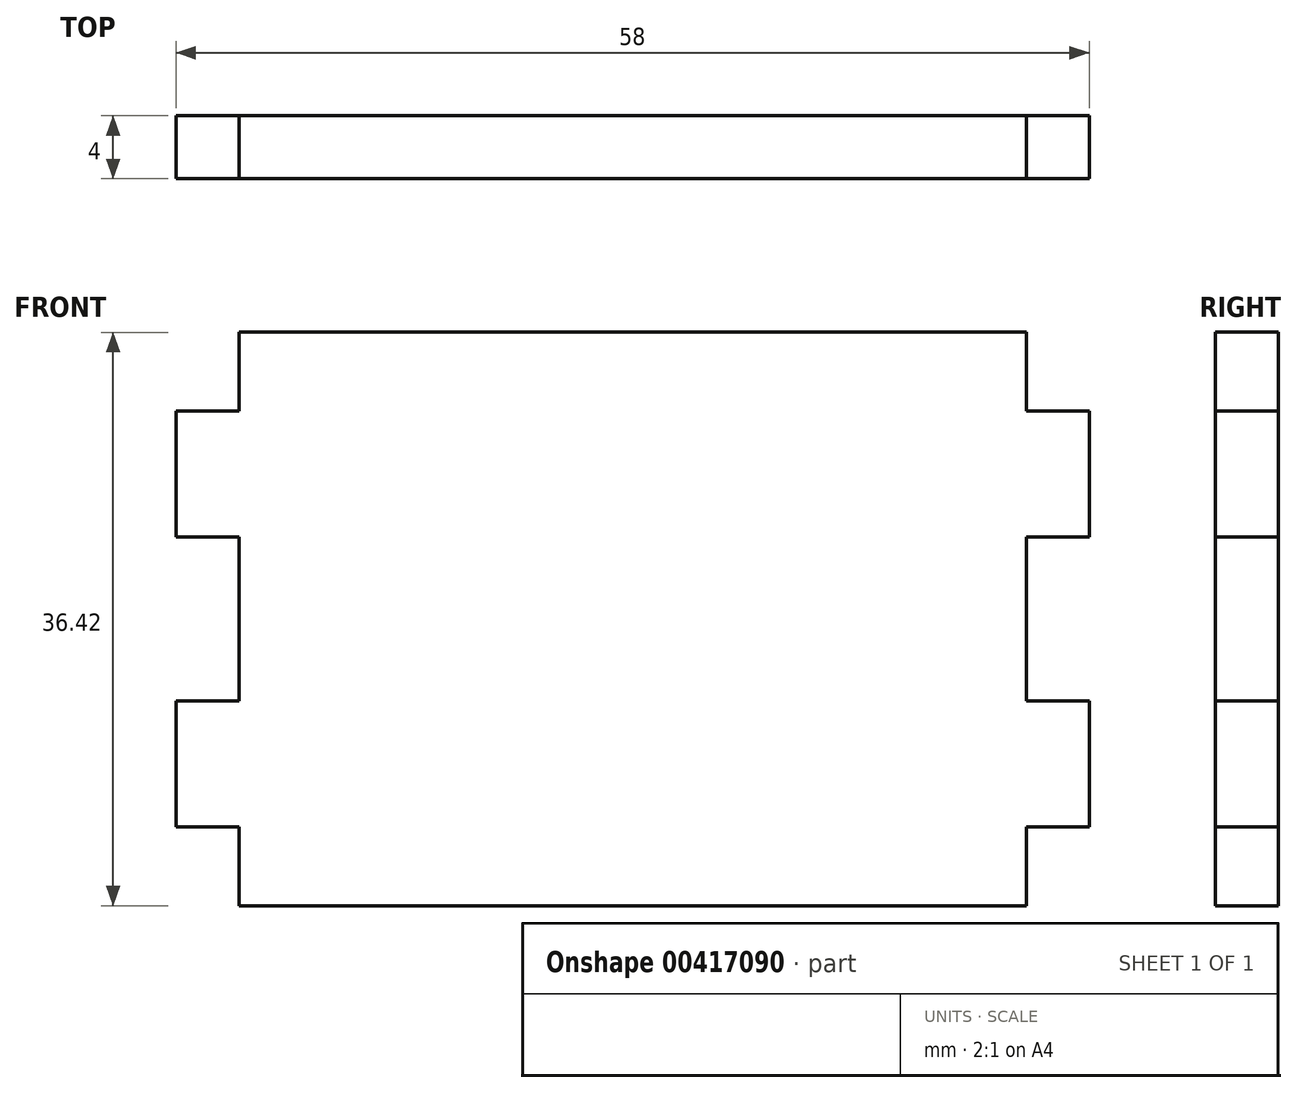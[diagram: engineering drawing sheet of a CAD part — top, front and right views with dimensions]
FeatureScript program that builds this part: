
annotation { "Feature Type Name" : "Feature", "Feature Type Description" : "" }
export const myFeature = defineFeature(function(context is Context, id is Id, definition is map)
    precondition{}
    {
        {
            var Q0;
            Q0=qCreatedBy(makeId("Front.planeOp"),FACE);
            var sketch = newSketch(context, id + "F0", { "sketchPlane" : qUnion([Q0])});
            skLineSegment(sketch, "E0", {"start": v(-25, 0) * mm, "end": v(-25, -5.21) * mm});
            skLineSegment(sketch, "E1", {"start": v(-25, -5.21) * mm, "end": v(-29, -5.21) * mm});
            skLineSegment(sketch, "E2", {"start": v(-29, -5.21) * mm, "end": v(-29, -13.21) * mm});
            skLineSegment(sketch, "E3", {"start": v(-29, -13.21) * mm, "end": v(-25, -13.21) * mm});
            skLineSegment(sketch, "E4", {"start": v(-25, -13.21) * mm, "end": v(-25, -18.21) * mm});
            skLineSegment(sketch, "E5", {"start": v(-25, -18.21) * mm, "end": v(0, -18.21) * mm});
            skLineSegment(sketch, "E6.MirrorCS", {"start": v(25, -13.21) * mm, "end": v(25, -18.21) * mm});
            skLineSegment(sketch, "E7.MirrorCS", {"start": v(29, -13.21) * mm, "end": v(25, -13.21) * mm});
            skLineSegment(sketch, "E8.MirrorCS", {"start": v(25, -5.21) * mm, "end": v(29, -5.21) * mm});
            skLineSegment(sketch, "E9.MirrorCS", {"start": v(25, -18.21) * mm, "end": v(0, -18.21) * mm});
            skLineSegment(sketch, "E10.MirrorCS", {"start": v(25, 0) * mm, "end": v(25, -5.21) * mm});
            skLineSegment(sketch, "E11.MirrorCS", {"start": v(29, -5.21) * mm, "end": v(29, -13.21) * mm});
            skLineSegment(sketch, "E12.MirrorCS", {"start": v(25, 5.21) * mm, "end": v(29, 5.21) * mm});
            skLineSegment(sketch, "E13.MirrorCS", {"start": v(29, 13.21) * mm, "end": v(25, 13.21) * mm});
            skLineSegment(sketch, "E14.MirrorCS", {"start": v(25, 13.21) * mm, "end": v(25, 18.21) * mm});
            skLineSegment(sketch, "E15.MirrorCS", {"start": v(-25, 5.21) * mm, "end": v(-29, 5.21) * mm});
            skLineSegment(sketch, "E16.MirrorCS", {"start": v(-25, 13.21) * mm, "end": v(-25, 18.21) * mm});
            skLineSegment(sketch, "E17.MirrorCS", {"start": v(29, 5.21) * mm, "end": v(29, 13.21) * mm});
            skLineSegment(sketch, "E18.MirrorCS", {"start": v(25, 0) * mm, "end": v(25, 5.21) * mm});
            skLineSegment(sketch, "E19.MirrorCS", {"start": v(25, 18.21) * mm, "end": v(0, 18.21) * mm});
            skLineSegment(sketch, "E20.MirrorCS", {"start": v(-29, 5.21) * mm, "end": v(-29, 13.21) * mm});
            skLineSegment(sketch, "E21.MirrorCS", {"start": v(-25, 0) * mm, "end": v(-25, 5.21) * mm});
            skLineSegment(sketch, "E22.MirrorCS", {"start": v(-29, 13.21) * mm, "end": v(-25, 13.21) * mm});
            skLineSegment(sketch, "E23.MirrorCS", {"start": v(-25, 18.21) * mm, "end": v(0, 18.21) * mm});
            skSolve(sketch);
        }
        {
            var Q0;
            Q0=makeQuery(id+"F0.imprint","IMPRINT",FACE,{"disambiguationData":[TD([[makeQuery(id+"F0.imprint","IMPRINT",EDGE,{"derivedFrom":sQuery(id+"F0.wireOp",EDGE,"E0")}),1.0]])]});
            extrude(context, id + "F1", {"entities" : qUnion([Q0]), "depth" : 4 * mm});
        }
    });
